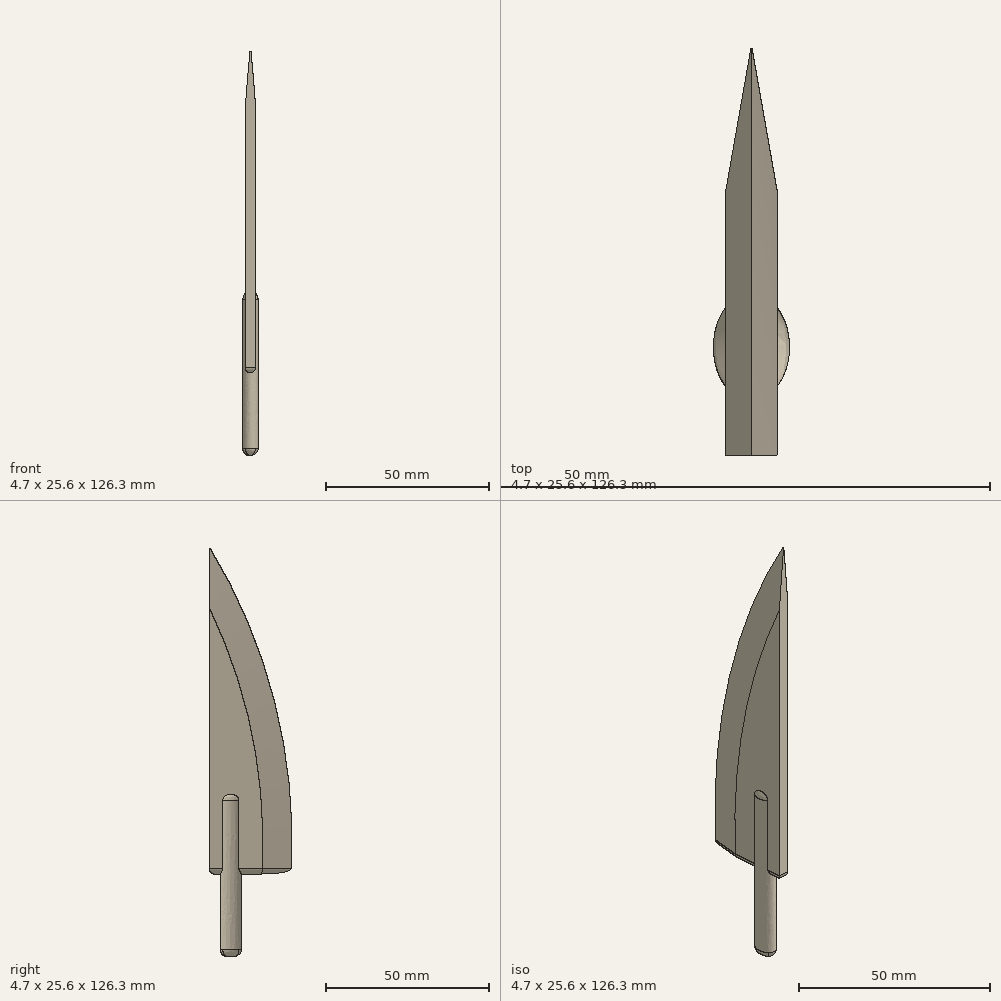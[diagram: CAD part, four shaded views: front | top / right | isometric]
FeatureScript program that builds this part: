
annotation { "Feature Type Name" : "Feature", "Feature Type Description" : "" }
export const myFeature = defineFeature(function(context is Context, id is Id, definition is map)
    precondition{}
    {
        {
            var Q0;
            Q0=qCreatedBy(makeId("Right.planeOp"),FACE);
            var sketch = newSketch(context, id + "F0", { "sketchPlane" : qUnion([Q0])});
            skLineSegment(sketch, "E0", {"start": v(0, 0) * mm, "end": v(12.7, 0) * mm});
            skLineSegment(sketch, "E1", {"start": v(12.7, 0) * mm, "end": v(0, 0) * mm});
            skLineSegment(sketch, "E2", {"start": v(0, 0) * mm, "end": v(-12.7, 0) * mm});
            skLineSegment(sketch, "E3", {"start": v(-12.7, 0) * mm, "end": v(-12.7, 101.13) * mm});
            skArc(sketch, "E4", {"start": v(12.7, 0) * mm, "mid": v(7.76, 52.51) * mm, "end": v(-12.7, 101.13) * mm});
            skSolve(sketch);
        }
        {
            var Q0;
            Q0 = qSketchRegion(id + "F0", true);
            extrude(context, id + "F1", {"entities" : qUnion([Q0]), "endBound" : BoundingType.SYMMETRIC, "depth" : 3.17 * mm});
        }
        {
            var Q0;
            Q0=makeQuery(id+"F1.opExtrude","CAP_EDGE",EDGE,{"disambiguationData":[OSD([sQuery(id+"F0.wireOp",EDGE,"E4")])],"isStart":false});
            var Q1;
            Q1=makeQuery(id+"F1.opExtrude","CAP_EDGE",EDGE,{"disambiguationData":[OSD([sQuery(id+"F0.wireOp",EDGE,"E4")])],"isStart":true});
            chamfer(context, id + "F2", {"entities" : qUnion([Q0, Q1]), "chamferType" : ChamferType.OFFSET_ANGLE, "width" : 9.14 * mm, "oppositeDirection" : false, "angle" : 10 * degree, "tangentPropagation" : true});
        }
        {
            var Q0;
            Q0=makeQuery(id+"F1.opExtrude","SWEPT_FACE",FACE,{"disambiguationData":[OSD([sQuery(id+"F0.wireOp",EDGE,"E1"),sQuery(id+"F0.wireOp",EDGE,"E2")])]});
            var sketch = newSketch(context, id + "F3", { "sketchPlane" : qUnion([Q0])});
            skLineSegment(sketch, "E5", {"start": v(0, 12.7) * mm, "end": v(0, 6.66) * mm});
            skPoint(sketch, "E5.endSnap0", {"position": v(0, 12.7) * mm});
            skLineSegment(sketch, "E6", {"start": v(0, 6.66) * mm, "end": v(0, 5.29) * mm});
            skEllipse(sketch, "E7", {"center": v(0, 5.97) * mm, "majorRadius": 2.37 * mm, "minorRadius": 3.32 * mm, "majorAxis": v(-1, 0)});
            skSolve(sketch);
        }
        {
            var Q0;
            {var subQ3=sQuery(id+"F3.wireOp",EDGE,"E7");var subQ8=makeQuery(id+"F3.imprint","INTERSECT",VERTEX,{"derivedFrom":[sQuery(id+"F3.wireOp",EDGE,"E5"),subQ3]});Q0=makeQuery(id+"F3.imprint","IMPRINT",FACE,{"disambiguationData":[TD([[makeQuery(id+"F3.imprint","IMPRINT",EDGE,{"disambiguationData":[TD([[subQ8,1.0]])],"derivedFrom":subQ3}),1.0]])]});}
            var Q1;
            {var subQ0=makeQuery(id+"F1.opExtrude","CAP_EDGE",EDGE,{"disambiguationData":[OSD([sQuery(id+"F0.wireOp",EDGE,"E1"),sQuery(id+"F0.wireOp",EDGE,"E2")])],"isStart":false});var subQ1=sQuery(id+"F3.wireOp",EDGE,"E7");var subQ3=makeQuery(id+"F3.imprint","INTERSECT",VERTEX,{"disambiguationData":[OD(0.0)],"derivedFrom":[subQ0,subQ1]});Q1=makeQuery(id+"F3.imprint","IMPRINT",FACE,{"disambiguationData":[TD([[makeQuery(id+"F3.imprint","IMPRINT",EDGE,{"disambiguationData":[TD([[subQ3,1.0]])],"derivedFrom":subQ1}),1.0]])]});}
            var Q2;
            {var subQ0=makeQuery(id+"F1.opExtrude","CAP_EDGE",EDGE,{"disambiguationData":[OSD([sQuery(id+"F0.wireOp",EDGE,"E1"),sQuery(id+"F0.wireOp",EDGE,"E2")])],"isStart":true});var subQ1=sQuery(id+"F3.wireOp",EDGE,"E7");var subQ3=makeQuery(id+"F3.imprint","INTERSECT",VERTEX,{"disambiguationData":[OD(0.0)],"derivedFrom":[subQ0,subQ1]});Q2=makeQuery(id+"F3.imprint","IMPRINT",FACE,{"disambiguationData":[TD([[makeQuery(id+"F3.imprint","IMPRINT",EDGE,{"disambiguationData":[TD([[subQ3,-1.0]])],"derivedFrom":subQ1}),1.0]])]});}
            extrude(context, id + "F4", {"entities" : qUnion([Q0, Q1, Q2]), "operationType" : NewBodyOperationType.ADD, "endBound" : BoundingType.SYMMETRIC, "depth" : 50.8 * mm});
        }
        {
            var Q0;
            {var subQ0=sQuery(id+"F3.wireOp",EDGE,"E7");Q0=makeQuery(id+"F4.boolean.opBoolean","SPLIT",EDGE,{"disambiguationData":[TD([makeQuery(id+"F1.opExtrude","CAP_FACE",FACE,{"disambiguationData":[OSD([sQuery(id+"F0.wireOp",EDGE,"E1"),sQuery(id+"F0.wireOp",EDGE,"E2"),sQuery(id+"F0.wireOp",EDGE,"E3"),sQuery(id+"F0.wireOp",EDGE,"E4")])],"isStart":true})])],"derivedFrom":makeQuery(id+"F4.opExtrude","CAP_EDGE",EDGE,{"disambiguationData":[OSD([subQ0])],"isStart":true})});}
            var Q1;
            {var subQ0=sQuery(id+"F3.wireOp",EDGE,"E7");Q1=makeQuery(id+"F4.boolean.opBoolean","SPLIT",EDGE,{"disambiguationData":[TD([makeQuery(id+"F1.opExtrude","CAP_FACE",FACE,{"disambiguationData":[OSD([sQuery(id+"F0.wireOp",EDGE,"E1"),sQuery(id+"F0.wireOp",EDGE,"E2"),sQuery(id+"F0.wireOp",EDGE,"E3"),sQuery(id+"F0.wireOp",EDGE,"E4")])],"isStart":false})])],"derivedFrom":makeQuery(id+"F4.opExtrude","CAP_EDGE",EDGE,{"disambiguationData":[OSD([subQ0])],"isStart":true})});}
            fillet(context, id + "F5", {"entities" : qUnion([Q0, Q1]), "radius" : 2.8 * mm, "tangentPropagation" : true, "allowEdgeOverflow" : false});
        }
        {
            var Q0;
            {var subQ0=sQuery(id+"F0.wireOp",EDGE,"E1");var subQ1=sQuery(id+"F0.wireOp",EDGE,"E2");var subQ2=sQuery(id+"F0.wireOp",EDGE,"E4");Q0=makeQuery(id+"F4.boolean.opBoolean","SPLIT",EDGE,{"disambiguationData":[TD([makeQuery(id+"F2.opChamfer","BLEND_FACE",FACE,{"disambiguationData":[OSD([subQ2]),TDD([makeQuery(id+"F1.opExtrude","CAP_EDGE",EDGE,{"disambiguationData":[OSD([subQ2])],"isStart":false})])]})])],"derivedFrom":makeQuery(id+"F1.opExtrude","CAP_EDGE",EDGE,{"disambiguationData":[OSD([subQ0,subQ1])],"isStart":false})});}
            var Q1;
            Q1=makeQuery(id+"F2.opChamfer","BLEND_EDGE",EDGE,{"blendedFrom":[makeQuery(id+"F1.opExtrude","CAP_EDGE",EDGE,{"disambiguationData":[OSD([sQuery(id+"F0.wireOp",EDGE,"E4")])],"isStart":false}),makeQuery(id+"F1.opExtrude","SWEPT_FACE",FACE,{"disambiguationData":[OSD([sQuery(id+"F0.wireOp",EDGE,"E1"),sQuery(id+"F0.wireOp",EDGE,"E2")])]})],"blendedInto":[makeQuery(id+"F1.opExtrude","SWEPT_FACE",FACE,{"disambiguationData":[OSD([sQuery(id+"F0.wireOp",EDGE,"E1"),sQuery(id+"F0.wireOp",EDGE,"E2")])]})]});
            var Q2;
            {var subQ0=sQuery(id+"F0.wireOp",EDGE,"E1");var subQ1=sQuery(id+"F0.wireOp",EDGE,"E2");var subQ2=sQuery(id+"F0.wireOp",EDGE,"E4");Q2=makeQuery(id+"F4.boolean.opBoolean","SPLIT",EDGE,{"disambiguationData":[TD([makeQuery(id+"F2.opChamfer","BLEND_FACE",FACE,{"disambiguationData":[OSD([subQ2]),TDD([makeQuery(id+"F1.opExtrude","CAP_EDGE",EDGE,{"disambiguationData":[OSD([subQ2])],"isStart":true})])]})])],"derivedFrom":makeQuery(id+"F1.opExtrude","CAP_EDGE",EDGE,{"disambiguationData":[OSD([subQ0,subQ1])],"isStart":true})});}
            var Q3;
            Q3=makeQuery(id+"F2.opChamfer","BLEND_EDGE",EDGE,{"blendedFrom":[makeQuery(id+"F1.opExtrude","CAP_EDGE",EDGE,{"disambiguationData":[OSD([sQuery(id+"F0.wireOp",EDGE,"E4")])],"isStart":true}),makeQuery(id+"F1.opExtrude","SWEPT_FACE",FACE,{"disambiguationData":[OSD([sQuery(id+"F0.wireOp",EDGE,"E1"),sQuery(id+"F0.wireOp",EDGE,"E2")])]})],"blendedInto":[makeQuery(id+"F1.opExtrude","SWEPT_FACE",FACE,{"disambiguationData":[OSD([sQuery(id+"F0.wireOp",EDGE,"E1"),sQuery(id+"F0.wireOp",EDGE,"E2")])]})]});
            var Q4;
            {var subQ0=sQuery(id+"F0.wireOp",EDGE,"E1");var subQ1=sQuery(id+"F0.wireOp",EDGE,"E2");var subQ2=sQuery(id+"F0.wireOp",EDGE,"E3");Q4=makeQuery(id+"F4.boolean.opBoolean","SPLIT",EDGE,{"disambiguationData":[TD([makeQuery(id+"F1.opExtrude","SWEPT_FACE",FACE,{"disambiguationData":[OSD([subQ2])]})])],"derivedFrom":makeQuery(id+"F1.opExtrude","CAP_EDGE",EDGE,{"disambiguationData":[OSD([subQ0,subQ1])],"isStart":true})});}
            var Q5;
            Q5=makeQuery(id+"F1.opExtrude","SWEPT_EDGE",EDGE,{"disambiguationData":[OSD([sQuery(id+"F0.wireOp",EDGE,"E2"),sQuery(id+"F0.wireOp",EDGE,"E3")])]});
            var Q6;
            {var subQ0=sQuery(id+"F0.wireOp",EDGE,"E1");var subQ1=sQuery(id+"F0.wireOp",EDGE,"E2");var subQ2=sQuery(id+"F0.wireOp",EDGE,"E3");Q6=makeQuery(id+"F4.boolean.opBoolean","SPLIT",EDGE,{"disambiguationData":[TD([makeQuery(id+"F1.opExtrude","SWEPT_FACE",FACE,{"disambiguationData":[OSD([subQ2])]})])],"derivedFrom":makeQuery(id+"F1.opExtrude","CAP_EDGE",EDGE,{"disambiguationData":[OSD([subQ0,subQ1])],"isStart":false})});}
            fillet(context, id + "F6", {"entities" : qUnion([Q0, Q1, Q2, Q3, Q4, Q5, Q6]), "radius" : 1.57 * mm, "tangentPropagation" : true, "allowEdgeOverflow" : false});
        }
        {
            var Q0;
            Q0=makeQuery(id+"F4.opExtrude","CAP_EDGE",EDGE,{"disambiguationData":[OSD([sQuery(id+"F3.wireOp",EDGE,"E7")])],"isStart":false});
            fillet(context, id + "F7", {"entities" : qUnion([Q0]), "radius" : 2.03 * mm, "tangentPropagation" : true, "allowEdgeOverflow" : false});
        }
    });
